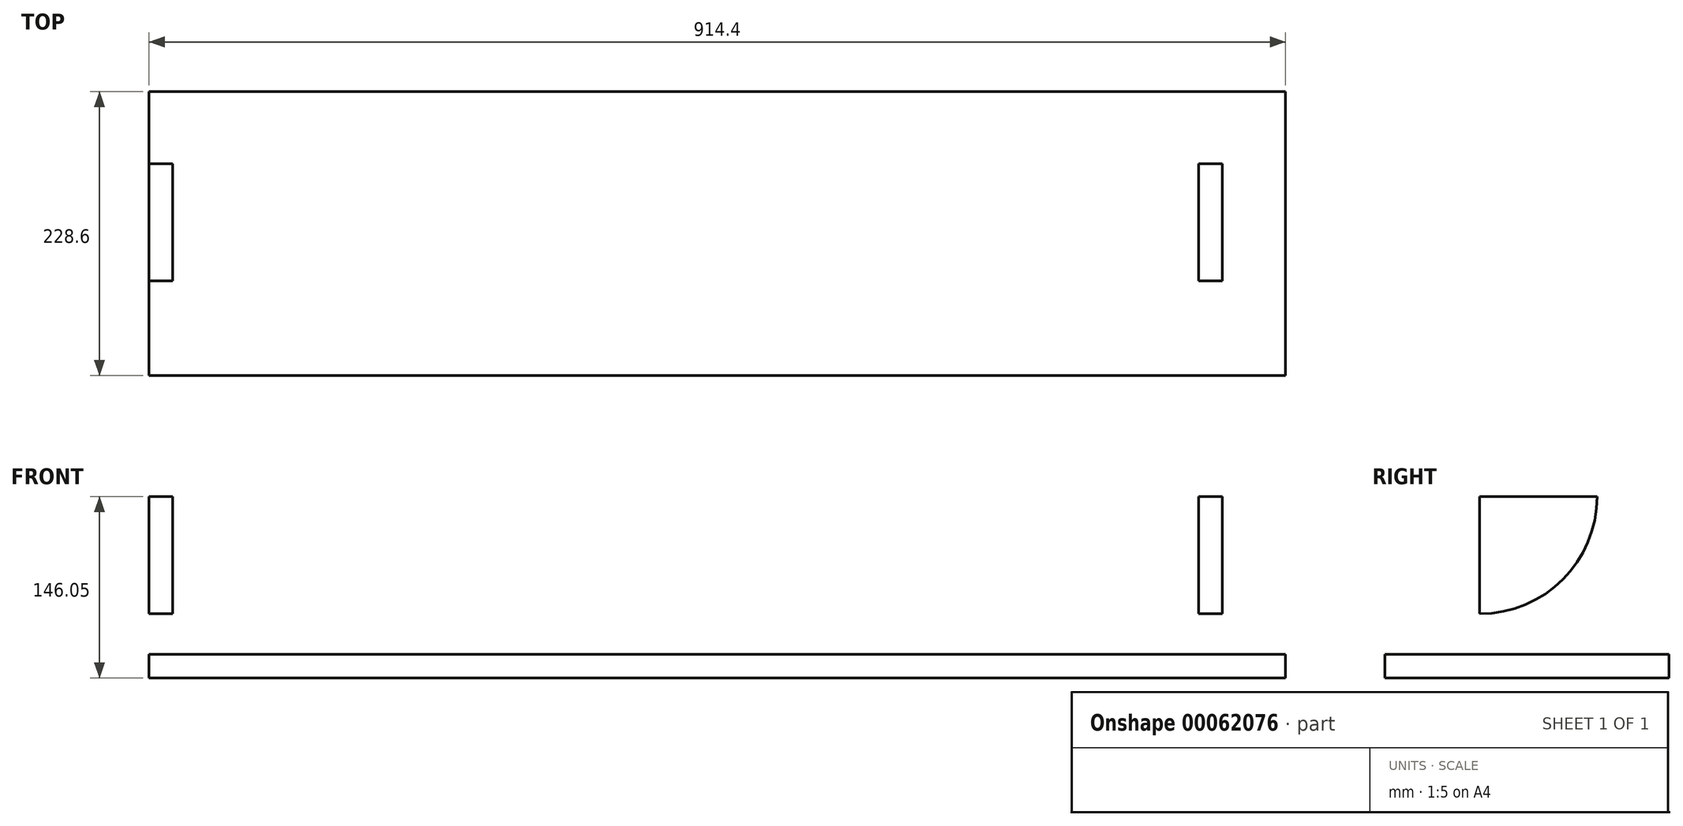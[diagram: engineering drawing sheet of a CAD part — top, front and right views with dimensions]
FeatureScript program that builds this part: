
annotation { "Feature Type Name" : "Feature", "Feature Type Description" : "" }
export const myFeature = defineFeature(function(context is Context, id is Id, definition is map)
    precondition{}
    {
        {
            var Q0;
            Q0=qCreatedBy(makeId("Front.planeOp"),FACE);
            var sketch = newSketch(context, id + "F0", { "sketchPlane" : qUnion([Q0])});
            skLineSegment(sketch, "E0.bottom", {"start": v(-457.2, 0) * mm, "end": v(457.2, 0) * mm});
            skLineSegment(sketch, "E0.top", {"start": v(-457.2, -19.05) * mm, "end": v(457.2, -19.05) * mm});
            skLineSegment(sketch, "E0.left", {"start": v(-457.2, 0) * mm, "end": v(-457.2, -19.05) * mm});
            skLineSegment(sketch, "E0.right", {"start": v(457.2, 0) * mm, "end": v(457.2, -19.05) * mm});
            skSolve(sketch);
        }
        {
            var Q0;
            Q0=makeQuery(id+"F0.imprint","IMPRINT",FACE,{"disambiguationData":[TD([[makeQuery(id+"F0.imprint","IMPRINT",EDGE,{"derivedFrom":sQuery(id+"F0.wireOp",EDGE,"E0.bottom")}),-1.0]])]});
            extrude(context, id + "F1", {"entities" : qUnion([Q0]), "depth" : 228.6 * mm});
        }
        {
            var Q0;
            Q0=makeQuery(id+"F1.opExtrude","SWEPT_FACE",FACE,{"disambiguationData":[OSD([sQuery(id+"F0.wireOp",EDGE,"E0.bottom")])]});
            var sketch = newSketch(context, id + "F2", { "sketchPlane" : qUnion([Q0])});
            skLineSegment(sketch, "E1.bottom", {"start": v(-457.2, 0) * mm, "end": v(-438.15, 0) * mm});
            skLineSegment(sketch, "E1.top", {"start": v(-457.2, -152.4) * mm, "end": v(-438.15, -152.4) * mm});
            skLineSegment(sketch, "E1.left", {"start": v(-457.2, 0) * mm, "end": v(-457.2, -152.4) * mm});
            skLineSegment(sketch, "E1.right", {"start": v(-438.15, 0) * mm, "end": v(-438.15, -152.4) * mm});
            skSolve(sketch);
        }
        {
            var Q0;
            Q0 = qSketchRegion(id + "F2", true);
            extrude(context, id + "F3", {"entities" : qUnion([Q0]), "depth" : 127 * mm});
        }
        {
            var Q0;
            Q0=makeQuery(id+"F3.opExtrude","SWEPT_FACE",FACE,{"disambiguationData":[OSD([sQuery(id+"F2.wireOp",EDGE,"E1.left")])]});
            var sketch = newSketch(context, id + "F4", { "sketchPlane" : qUnion([Q0])});
            skArc(sketch, "E2", {"start": v(152.4, 32.62) * mm, "mid": v(85.66, 60.26) * mm, "end": v(58.02, 127) * mm});
            skLineSegment(sketch, "E3", {"start": v(152.4, 127) * mm, "end": v(58.02, 127) * mm});
            skLineSegment(sketch, "E4", {"start": v(152.4, 127) * mm, "end": v(152.4, 32.62) * mm});
            skSolve(sketch);
        }
        {
            var Q0;
            Q0=makeQuery(id+"F4.imprint","IMPRINT",FACE,{"disambiguationData":[TD([[makeQuery(id+"F4.imprint","IMPRINT",EDGE,{"derivedFrom":sQuery(id+"F4.wireOp",EDGE,"E2")}),-1.0]])]});
            extrude(context, id + "F5", {"entities" : qUnion([Q0]), "operationType" : NewBodyOperationType.REMOVE, "endBound" : BoundingType.UP_TO_NEXT, "oppositeDirection" : true, "depth" : 25.4 * mm});
        }
        {
            var Q0;
            Q0=makeQuery(id+"F3.opExtrude","SWEPT_BODY",BODY,{"disambiguationData":[OSD([sQuery(id+"F2.wireOp",EDGE,"E1.bottom"),sQuery(id+"F2.wireOp",EDGE,"E1.top"),sQuery(id+"F2.wireOp",EDGE,"E1.left"),sQuery(id+"F2.wireOp",EDGE,"E1.right")])]});
            transform(context, id + "F6", {"entities" : qUnion([Q0]), "transformType" : TransformType.TRANSLATION_3D, "dx" : 844.55 * mm, "dy" : 0 * mm, "dz" : 0 * mm, "makeCopy" : true});
        }
    });
